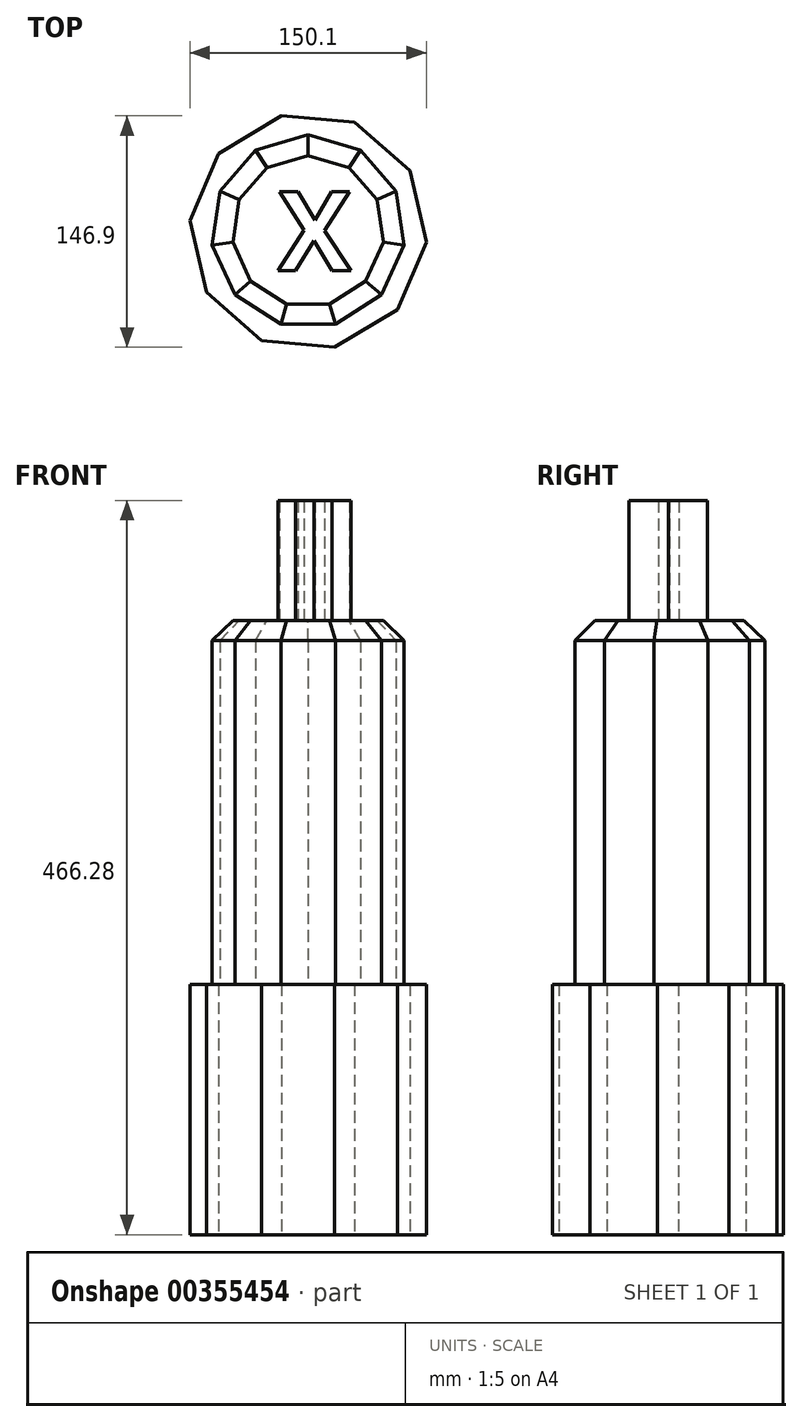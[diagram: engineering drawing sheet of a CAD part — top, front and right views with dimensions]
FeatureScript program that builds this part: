
annotation { "Feature Type Name" : "Feature", "Feature Type Description" : "" }
export const myFeature = defineFeature(function(context is Context, id is Id, definition is map)
    precondition{}
    {
        {
            var Q0;
            Q0=qCreatedBy(makeId("Top.planeOp"),FACE);
            var sketch = newSketch(context, id + "F0", { "sketchPlane" : qUnion([Q0])});
            skCircle(sketch, "E0.cCircle", {"center": v(0, 0) * mm, "radius": 60.32 * mm, "construction": true});
            skLineSegment(sketch, "E0.0", {"start": v(48.78, 35.47) * mm, "end": v(55.11, -24.51) * mm});
            skLineSegment(sketch, "E0.1", {"start": v(55.11, -24.51) * mm, "end": v(6.33, -59.98) * mm});
            skLineSegment(sketch, "E0.2", {"start": v(6.33, -59.98) * mm, "end": v(-48.78, -35.47) * mm});
            skLineSegment(sketch, "E0.3", {"start": v(-48.78, -35.47) * mm, "end": v(-55.11, 24.51) * mm});
            skLineSegment(sketch, "E0.4", {"start": v(-55.11, 24.51) * mm, "end": v(-6.33, 59.98) * mm});
            skLineSegment(sketch, "E0.5", {"start": v(-6.33, 59.98) * mm, "end": v(48.78, 35.47) * mm});
            skSolve(sketch);
        }
        {
            var Q0;
            Q0=makeQuery(id+"F0.imprint","IMPRINT",FACE,{"disambiguationData":[TD([[makeQuery(id+"F0.imprint","IMPRINT",EDGE,{"derivedFrom":sQuery(id+"F0.wireOp",EDGE,"E0.0")}),-1.0]])]});
            extrude(context, id + "F1", {"entities" : qUnion([Q0]), "depth" : 107.97 * mm});
        }
        {
            var Q0;
            Q0=makeQuery(id+"F1.opExtrude","CAP_FACE",FACE,{"disambiguationData":[OSD([sQuery(id+"F0.wireOp",EDGE,"E0.0"),sQuery(id+"F0.wireOp",EDGE,"E0.1"),sQuery(id+"F0.wireOp",EDGE,"E0.2"),sQuery(id+"F0.wireOp",EDGE,"E0.3"),sQuery(id+"F0.wireOp",EDGE,"E0.4"),sQuery(id+"F0.wireOp",EDGE,"E0.5")])],"isStart":false});
            var sketch = newSketch(context, id + "F2", { "sketchPlane" : qUnion([Q0])});
            skCircle(sketch, "E1", {"center": v(0, 0) * mm, "radius": 29.16 * mm});
            skSolve(sketch);
        }
        {
            var Q0;
            Q0=sQuery(id+"F2.wireOp",EDGE,"E1");
            extrude(context, id + "F3", {"bodyType" : ToolBodyType.SURFACE, "surfaceEntities" : qUnion([Q0]), "depth" : 119.74 * mm});
        }
        {
            var Q0;
            Q0=makeQuery(id+"F1.opExtrude","SWEPT_BODY",BODY,{"disambiguationData":[OSD([sQuery(id+"F0.wireOp",EDGE,"E0.0"),sQuery(id+"F0.wireOp",EDGE,"E0.1"),sQuery(id+"F0.wireOp",EDGE,"E0.2"),sQuery(id+"F0.wireOp",EDGE,"E0.3"),sQuery(id+"F0.wireOp",EDGE,"E0.4"),sQuery(id+"F0.wireOp",EDGE,"E0.5")])]});
            deleteBodies(context, id + "F4", {"entities" : qUnion([Q0])});
        }
        {
            var Q0;
            Q0=makeQuery(id+"F3.opExtrude","SWEPT_BODY",BODY,{"disambiguationData":[OSD([sQuery(id+"F2.wireOp",EDGE,"E1")])]});
            deleteBodies(context, id + "F5", {"entities" : qUnion([Q0])});
        }
        {
            var Q0;
            Q0=qCreatedBy(makeId("Top.planeOp"),FACE);
            var sketch = newSketch(context, id + "F6", { "sketchPlane" : qUnion([Q0])});
            skCircle(sketch, "E2.cCircle", {"center": v(0, 0) * mm, "radius": 75.35 * mm, "construction": true});
            skLineSegment(sketch, "E2.0", {"start": v(56.78, -49.54) * mm, "end": v(16.81, -73.45) * mm});
            skLineSegment(sketch, "E2.1", {"start": v(16.81, -73.45) * mm, "end": v(-29.57, -69.3) * mm});
            skLineSegment(sketch, "E2.2", {"start": v(-29.57, -69.3) * mm, "end": v(-64.66, -38.69) * mm});
            skLineSegment(sketch, "E2.3", {"start": v(-64.66, -38.69) * mm, "end": v(-75.05, 6.7) * mm});
            skLineSegment(sketch, "E2.4", {"start": v(-75.05, 6.7) * mm, "end": v(-56.78, 49.54) * mm});
            skLineSegment(sketch, "E2.5", {"start": v(-56.78, 49.54) * mm, "end": v(-16.81, 73.45) * mm});
            skLineSegment(sketch, "E2.6", {"start": v(-16.81, 73.45) * mm, "end": v(29.57, 69.3) * mm});
            skLineSegment(sketch, "E2.7", {"start": v(29.57, 69.3) * mm, "end": v(64.66, 38.69) * mm});
            skLineSegment(sketch, "E2.8", {"start": v(64.66, 38.69) * mm, "end": v(75.05, -6.7) * mm});
            skLineSegment(sketch, "E2.9", {"start": v(75.05, -6.7) * mm, "end": v(56.78, -49.54) * mm});
            skSolve(sketch);
        }
        {
            var Q0;
            Q0=makeQuery(id+"F6.imprint","IMPRINT",FACE,{"disambiguationData":[TD([[makeQuery(id+"F6.imprint","IMPRINT",EDGE,{"derivedFrom":sQuery(id+"F6.wireOp",EDGE,"E2.0")}),-1.0]])]});
            var sketch = newSketch(context, id + "F7", { "sketchPlane" : qUnion([Q0])});
            skSolve(sketch);
        }
        {
            var Q0;
            Q0=makeQuery(id+"F7.imprint","IMPRINT",FACE,{"disambiguationData":[TD([[makeQuery(id+"F7.imprint","IMPRINT",EDGE,{"derivedFrom":makeQuery(id+"F6.imprint","IMPRINT",EDGE,{"derivedFrom":sQuery(id+"F6.wireOp",EDGE,"E2.0")})}),-1.0]])]});
            extrude(context, id + "F8", {"entities" : qUnion([Q0]), "depth" : 159.1 * mm});
        }
        {
            var Q0;
            Q0=makeQuery(id+"F8.opExtrude","CAP_FACE",FACE,{"disambiguationData":[OSD([sQuery(id+"F6.wireOp",EDGE,"E2.0"),sQuery(id+"F6.wireOp",EDGE,"E2.1"),sQuery(id+"F6.wireOp",EDGE,"E2.2"),sQuery(id+"F6.wireOp",EDGE,"E2.3"),sQuery(id+"F6.wireOp",EDGE,"E2.4"),sQuery(id+"F6.wireOp",EDGE,"E2.5"),sQuery(id+"F6.wireOp",EDGE,"E2.6"),sQuery(id+"F6.wireOp",EDGE,"E2.7"),sQuery(id+"F6.wireOp",EDGE,"E2.8"),sQuery(id+"F6.wireOp",EDGE,"E2.9")])],"isStart":false});
            var sketch = newSketch(context, id + "F9", { "sketchPlane" : qUnion([Q0])});
            skCircle(sketch, "E3.cCircle", {"center": v(0, 0) * mm, "radius": 61.5 * mm, "construction": true});
            skPoint(sketch, "E3.cCircle.perimeterSnap0", {"position": v(-36.8, 61.5) * mm});
            skLineSegment(sketch, "E3.0", {"start": v(0, 61.5) * mm, "end": v(33.25, 51.73) * mm});
            skPoint(sketch, "E3.0.startSnap0", {"position": v(-36.8, 61.5) * mm});
            skLineSegment(sketch, "E3.1", {"start": v(33.25, 51.73) * mm, "end": v(55.94, 25.55) * mm});
            skLineSegment(sketch, "E3.2", {"start": v(55.94, 25.55) * mm, "end": v(60.87, -8.75) * mm});
            skLineSegment(sketch, "E3.3", {"start": v(60.87, -8.75) * mm, "end": v(46.47, -40.27) * mm});
            skLineSegment(sketch, "E3.4", {"start": v(46.47, -40.27) * mm, "end": v(17.33, -59) * mm});
            skLineSegment(sketch, "E3.5", {"start": v(17.33, -59) * mm, "end": v(-17.33, -59) * mm});
            skLineSegment(sketch, "E3.6", {"start": v(-17.33, -59) * mm, "end": v(-46.47, -40.27) * mm});
            skLineSegment(sketch, "E3.7", {"start": v(-46.47, -40.27) * mm, "end": v(-60.87, -8.75) * mm});
            skLineSegment(sketch, "E3.8", {"start": v(-60.87, -8.75) * mm, "end": v(-55.94, 25.55) * mm});
            skLineSegment(sketch, "E3.9", {"start": v(-55.94, 25.55) * mm, "end": v(-33.25, 51.73) * mm});
            skLineSegment(sketch, "E3.10", {"start": v(-33.25, 51.73) * mm, "end": v(0, 61.5) * mm});
            skSolve(sketch);
        }
        {
            var Q0;
            Q0=makeQuery(id+"F9.imprint","IMPRINT",FACE,{"disambiguationData":[TD([[makeQuery(id+"F9.imprint","IMPRINT",EDGE,{"derivedFrom":sQuery(id+"F9.wireOp",EDGE,"E3.0")}),-1.0]])]});
            var Q1;
            Q1=sQuery(id+"F9.wireOp",EDGE,"E3.8");
            var Q2;
            Q2=sQuery(id+"F9.wireOp",EDGE,"E3.6");
            extrude(context, id + "F10", {"entities" : qUnion([Q0]), "operationType" : NewBodyOperationType.ADD, "surfaceEntities" : qUnion([Q1, Q2]), "depth" : 231 * mm});
        }
        {
            var Q0;
            Q0=makeQuery(id+"F10.opExtrude","CAP_FACE",FACE,{"disambiguationData":[OSD([sQuery(id+"F9.wireOp",EDGE,"E3.0"),sQuery(id+"F9.wireOp",EDGE,"E3.1"),sQuery(id+"F9.wireOp",EDGE,"E3.2"),sQuery(id+"F9.wireOp",EDGE,"E3.3"),sQuery(id+"F9.wireOp",EDGE,"E3.4"),sQuery(id+"F9.wireOp",EDGE,"E3.5"),sQuery(id+"F9.wireOp",EDGE,"E3.6"),sQuery(id+"F9.wireOp",EDGE,"E3.7"),sQuery(id+"F9.wireOp",EDGE,"E3.8"),sQuery(id+"F9.wireOp",EDGE,"E3.9"),sQuery(id+"F9.wireOp",EDGE,"E3.10")])],"isStart":false});
            var sketch = newSketch(context, id + "F11", { "sketchPlane" : qUnion([Q0])});
            skText(sketch, "E4", { "text": "X", "fontName": "OpenSans-Bold.ttf"});
            const initialGuessF11  = {"E4": [-0.01925, -0.02481, 1, 0, 0.05036]};
            skSetInitialGuess(sketch, initialGuessF11);
            skSolve(sketch);
        }
        {
            var Q0;
            Q0=makeQuery(id+"F11.imprint","IMPRINT",FACE,{"disambiguationData":[TD([[makeQuery(id+"F11.imprint","IMPRINT",EDGE,{"derivedFrom":sQuery(id+"F11.wireOp",EDGE,"E4.sketch_text.stroke-0")}),-1.0]])]});
            extrude(context, id + "F12", {"entities" : qUnion([Q0]), "operationType" : NewBodyOperationType.ADD, "depth" : 76.2 * mm});
        }
        {
            var Q0;
            Q0=makeQuery(id+"F10.opExtrude","CAP_EDGE",EDGE,{"disambiguationData":[OSD([sQuery(id+"F9.wireOp",EDGE,"E3.10")])],"isStart":false});
            var Q1;
            Q1=makeQuery(id+"F10.opExtrude","CAP_EDGE",EDGE,{"disambiguationData":[OSD([sQuery(id+"F9.wireOp",EDGE,"E3.9")])],"isStart":false});
            var Q2;
            Q2=makeQuery(id+"F10.opExtrude","CAP_EDGE",EDGE,{"disambiguationData":[OSD([sQuery(id+"F9.wireOp",EDGE,"E3.8")])],"isStart":false});
            var Q3;
            Q3=makeQuery(id+"F10.opExtrude","CAP_EDGE",EDGE,{"disambiguationData":[OSD([sQuery(id+"F9.wireOp",EDGE,"E3.7")])],"isStart":false});
            var Q4;
            Q4=makeQuery(id+"F10.opExtrude","CAP_EDGE",EDGE,{"disambiguationData":[OSD([sQuery(id+"F9.wireOp",EDGE,"E3.6")])],"isStart":false});
            var Q5;
            Q5=makeQuery(id+"F10.opExtrude","CAP_EDGE",EDGE,{"disambiguationData":[OSD([sQuery(id+"F9.wireOp",EDGE,"E3.5")])],"isStart":false});
            var Q6;
            Q6=makeQuery(id+"F10.opExtrude","CAP_EDGE",EDGE,{"disambiguationData":[OSD([sQuery(id+"F9.wireOp",EDGE,"E3.4")])],"isStart":false});
            var Q7;
            Q7=makeQuery(id+"F10.opExtrude","CAP_EDGE",EDGE,{"disambiguationData":[OSD([sQuery(id+"F9.wireOp",EDGE,"E3.3")])],"isStart":false});
            var Q8;
            Q8=makeQuery(id+"F10.opExtrude","CAP_EDGE",EDGE,{"disambiguationData":[OSD([sQuery(id+"F9.wireOp",EDGE,"E3.2")])],"isStart":false});
            var Q9;
            Q9=makeQuery(id+"F10.opExtrude","CAP_EDGE",EDGE,{"disambiguationData":[OSD([sQuery(id+"F9.wireOp",EDGE,"E3.1")])],"isStart":false});
            var Q10;
            Q10=makeQuery(id+"F10.opExtrude","CAP_EDGE",EDGE,{"disambiguationData":[OSD([sQuery(id+"F9.wireOp",EDGE,"E3.0")])],"isStart":false});
            chamfer(context, id + "F13", {"entities" : qUnion([Q0, Q1, Q2, Q3, Q4, Q5, Q6, Q7, Q8, Q9, Q10]), "width" : 12.7 * mm, "tangentPropagation" : true});
        }
        {
            var Q0;
            Q0=makeQuery(id+"F10.opExtrude","SWEPT_FACE",FACE,{"disambiguationData":[OSD([sQuery(id+"F9.wireOp",EDGE,"E3.10")])]});
            var sketch = newSketch(context, id + "F14", { "sketchPlane" : qUnion([Q0])});
            skPoint(sketch, "E5", {"position": v(0, 253.36) * mm});
            skSolve(sketch);
        }
        {
            var Q0;
            {var subQ0=sQuery(id+"F9.wireOp",EDGE,"E3.10");Q0=makeQuery(id+"F14.imprint","IMPRINT",FACE,{"disambiguationData":[TD([[makeQuery(id+"F14.imprint","IMPRINT",EDGE,{"derivedFrom":makeQuery(id+"F10.opExtrude","CAP_EDGE",EDGE,{"disambiguationData":[OSD([subQ0])],"isStart":true})}),-1.0]])]});}
            var sketch = newSketch(context, id + "F15", { "sketchPlane" : qUnion([Q0])});
            skSolve(sketch);
        }
        {
            var Q0;
            Q0=makeQuery(id+"F10.opExtrude","SWEPT_FACE",FACE,{"disambiguationData":[OSD([sQuery(id+"F9.wireOp",EDGE,"E3.0")])]});
            var sketch = newSketch(context, id + "F16", { "sketchPlane" : qUnion([Q0])});
            skLineSegment(sketch, "E6", {"start": v(0, 302.45) * mm, "end": v(-17.33, 281.8) * mm});
            skLineSegment(sketch, "E7", {"start": v(-17.33, 281.8) * mm, "end": v(4.98, 286.29) * mm});
            skLineSegment(sketch, "E8", {"start": v(4.98, 286.29) * mm, "end": v(1.57, 301.64) * mm});
            skLineSegment(sketch, "E9", {"start": v(1.57, 301.64) * mm, "end": v(0, 302.45) * mm});
            skSolve(sketch);
        }
        {
            var Q0;
            {var subQ0=sQuery(id+"F9.wireOp",EDGE,"E3.10");Q0=makeQuery(id+"F15.imprint","IMPRINT",FACE,{"disambiguationData":[TD([[makeQuery(id+"F15.imprint","IMPRINT",EDGE,{"derivedFrom":makeQuery(id+"F14.imprint","IMPRINT",EDGE,{"derivedFrom":makeQuery(id+"F10.opExtrude","CAP_EDGE",EDGE,{"disambiguationData":[OSD([subQ0])],"isStart":true})})}),-1.0]])]});}
            var sketch = newSketch(context, id + "F17", { "sketchPlane" : qUnion([Q0])});
            skFitSpline(sketch, "E10", {"points": [v(0, 352.05) * mm, v(13.93, 322.62) * mm, v(46.3, 352.5) * mm], "startDerivative": vector(23.2, -91.22) * mm, "endDerivative": vector(68.27, 87.64) * mm});
            skSolve(sketch);
        }
    });
